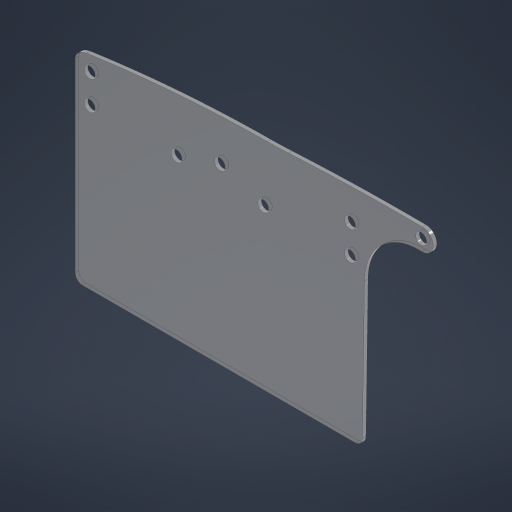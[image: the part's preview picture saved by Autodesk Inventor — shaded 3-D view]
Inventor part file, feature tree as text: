
AUTODESK INVENTOR PART (.ipt)
format: ipt  version: 2024 (Build 280153000, 153)  size: 267,264 bytes
history: native  units: in
note: dims shown in document units (in); Inventor stores cm internally (conversion verified against a paired STEP export)
features: sketch x3, extrude x1, hole x1, other x1
ambient origin geometry x8: Origin, YZ Plane, XZ Plane, XY Plane, X Axis, Y Axis, Z Axis, Center Point
bodies: Solid1 (feature_tree)
feature tree (6):
  extrude  "Extrusion1"  Depth=0.0625in
  hole  "Hole1"  [1 undecoded]
  other  "Bend Part1"
  sketch  "Sketch1"  dims[d2=0.0625in d3=0.0in d4=0.5in]
  sketch  "Sketch2"  dims[d5=0.25in d6=0.5in]
  sketch  "Sketch3"  dims[d7=4.5in d8=0.1875in d9=0.75in d10=0.375in d11=0.25in d12=0.5635in d13=1.0in d14=0.8108in d15=0.25in d23=1.0in d24=1.0in d25=0.25in d27=0.0in d28=1.5in d29=0.125in d31=0.125in d32=0.125in d33=0.98in d34=1.5in d35=1.5in d36=1.25in d37=0.25in d38=45.0deg d39=0.375in d40=8.0in d41=1.0in d42=2.5in d43=0.125in]
note: 1 required parameter value undecoded (feature->parameter linkage not recoverable at this tier; creation-order binding heuristic only, values carry confidence <= 0.55)
